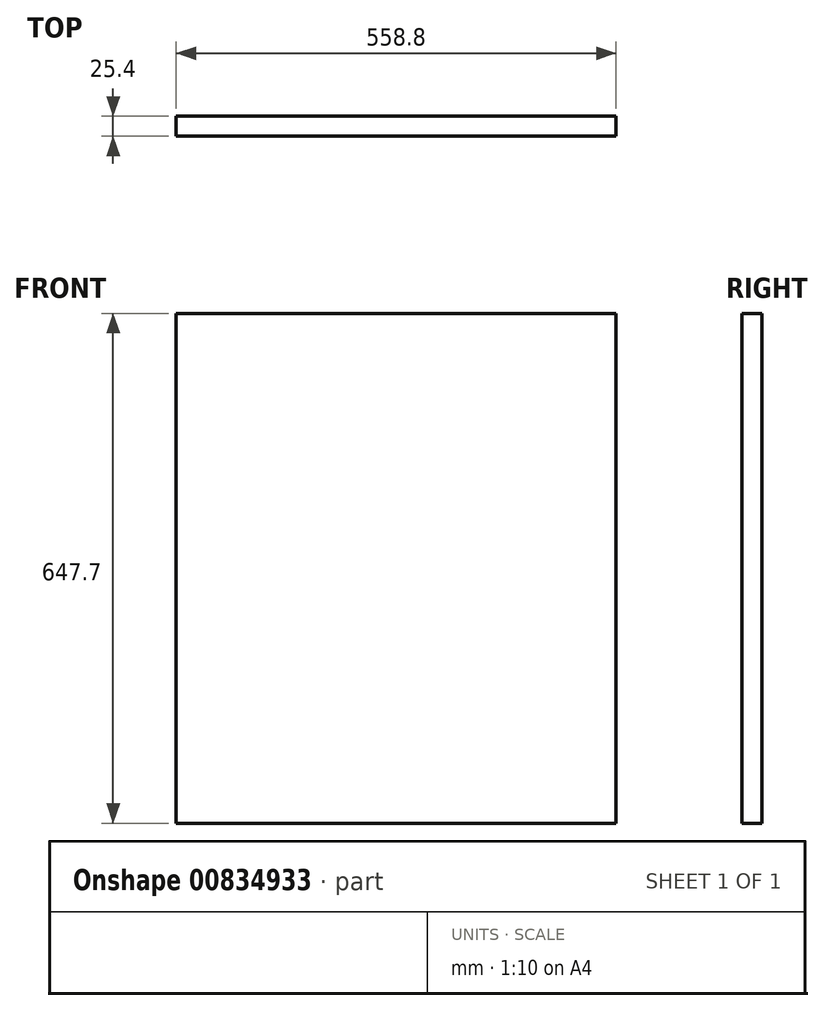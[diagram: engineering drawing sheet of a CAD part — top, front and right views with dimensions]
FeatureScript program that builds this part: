
annotation { "Feature Type Name" : "Feature", "Feature Type Description" : "" }
export const myFeature = defineFeature(function(context is Context, id is Id, definition is map)
    precondition{}
    {
        {
            var Q0;
            Q0=qCreatedBy(makeId("Front.planeOp"),FACE);
            var sketch = newSketch(context, id + "F0", { "sketchPlane" : qUnion([Q0])});
            skLineSegment(sketch, "E0.bottom", {"start": v(279.4, 323.85) * mm, "end": v(-279.4, 323.85) * mm});
            skLineSegment(sketch, "E0.top", {"start": v(279.4, -323.85) * mm, "end": v(-279.4, -323.85) * mm});
            skLineSegment(sketch, "E0.left", {"start": v(279.4, 323.85) * mm, "end": v(279.4, -323.85) * mm});
            skLineSegment(sketch, "E0.right", {"start": v(-279.4, 323.85) * mm, "end": v(-279.4, -323.85) * mm});
            skPoint(sketch, "E0.middle", {"position": v(0, 0) * mm});
            skSolve(sketch);
        }
        {
            var Q0;
            Q0=makeQuery(id+"F0.imprint","IMPRINT",FACE,{"disambiguationData":[TD([[makeQuery(id+"F0.imprint","IMPRINT",EDGE,{"derivedFrom":sQuery(id+"F0.wireOp",EDGE,"E0.bottom")}),1.0]])]});
            extrude(context, id + "F1", {"entities" : qUnion([Q0]), "depth" : 25.4 * mm, "offsetDistance" : 25.4 * mm});
        }
    });
